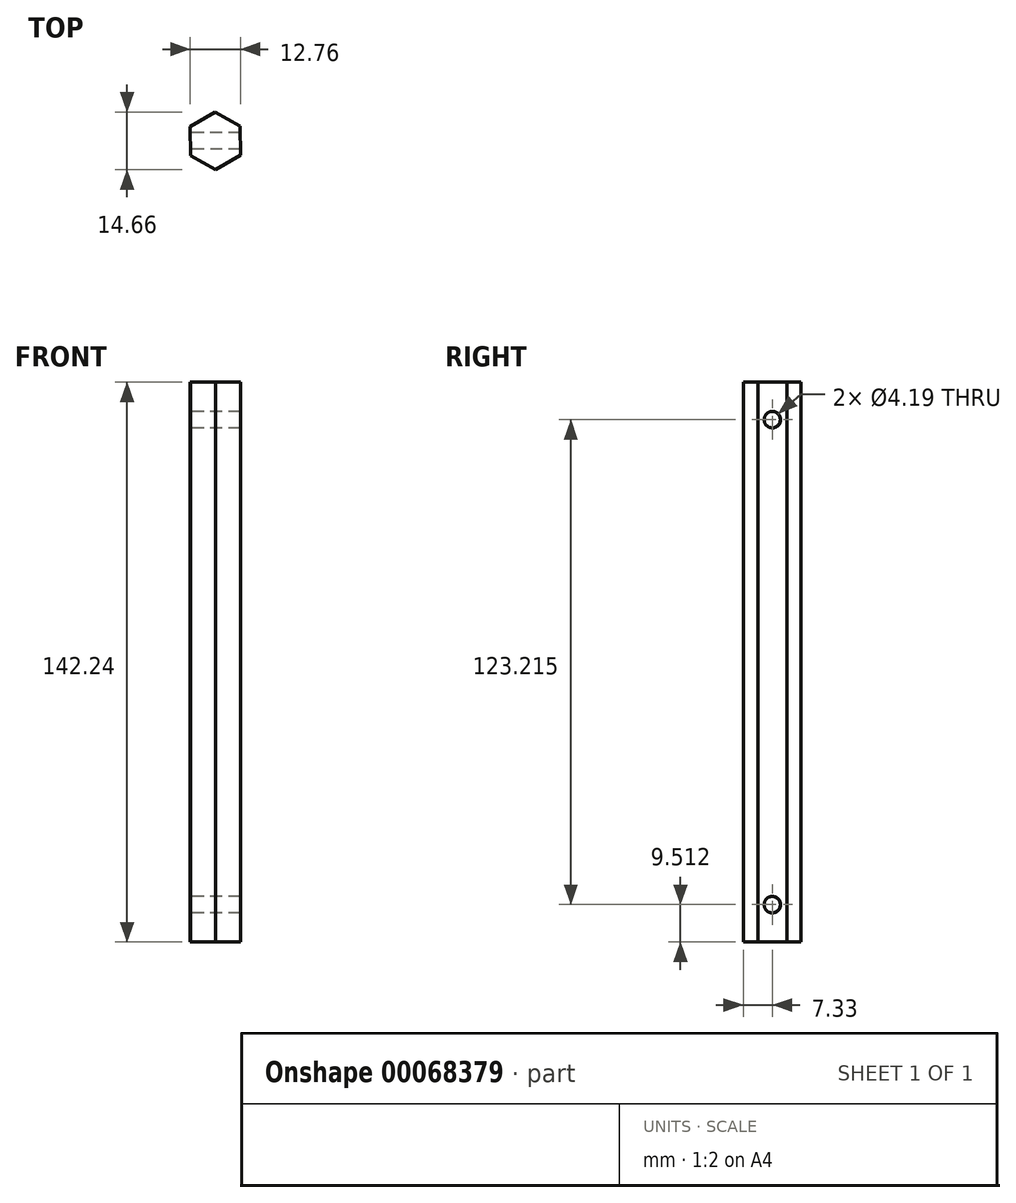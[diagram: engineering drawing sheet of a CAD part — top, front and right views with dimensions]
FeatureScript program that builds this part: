
annotation { "Feature Type Name" : "Feature", "Feature Type Description" : "" }
export const myFeature = defineFeature(function(context is Context, id is Id, definition is map)
    precondition{}
    {
        {
            var Q0;
            Q0=qCreatedBy(makeId("Top.planeOp"),FACE);
            var sketch = newSketch(context, id + "F0", { "sketchPlane" : qUnion([Q0])});
            skCircle(sketch, "E0.cCircle", {"center": v(0, 0) * mm, "radius": 6.35 * mm, "construction": true});
            skLineSegment(sketch, "E0.0", {"start": v(6.38, -3.62) * mm, "end": v(0.05, -7.33) * mm});
            skLineSegment(sketch, "E0.1", {"start": v(0.05, -7.33) * mm, "end": v(-6.32, -3.71) * mm});
            skLineSegment(sketch, "E0.2", {"start": v(-6.32, -3.71) * mm, "end": v(-6.38, 3.62) * mm});
            skLineSegment(sketch, "E0.3", {"start": v(-6.38, 3.62) * mm, "end": v(-0.05, 7.33) * mm});
            skLineSegment(sketch, "E0.4", {"start": v(-0.05, 7.33) * mm, "end": v(6.32, 3.71) * mm});
            skLineSegment(sketch, "E0.5", {"start": v(6.32, 3.71) * mm, "end": v(6.38, -3.62) * mm});
            skPoint(sketch, "E0.0.midPoint", {"position": v(3.22, -5.48) * mm});
            skSolve(sketch);
        }
        {
            var Q0;
            Q0=makeQuery(id+"F0.imprint","IMPRINT",FACE,{"disambiguationData":[TD([[makeQuery(id+"F0.imprint","IMPRINT",EDGE,{"derivedFrom":sQuery(id+"F0.wireOp",EDGE,"E0.0")}),-1.0]])]});
            extrude(context, id + "F1", {"entities" : qUnion([Q0]), "depth" : 142.24 * mm});
        }
        {
            var Q0;
            Q0=makeQuery(id+"F1.opExtrude","SWEPT_FACE",FACE,{"disambiguationData":[OSD([sQuery(id+"F0.wireOp",EDGE,"E0.2")])]});
            var sketch = newSketch(context, id + "F2", { "sketchPlane" : qUnion([Q0])});
            skCircle(sketch, "E1", {"center": v(0, 9.51) * mm, "radius": 2.1 * mm});
            skCircle(sketch, "E2", {"center": v(0, 132.73) * mm, "radius": 2.1 * mm});
            skPoint(sketch, "E2.centerSnap0", {"position": v(0, 142.24) * mm});
            skSolve(sketch);
        }
        {
            var Q0;
            Q0=makeQuery(id+"F2.imprint","IMPRINT",FACE,{"disambiguationData":[TD([[makeQuery(id+"F2.imprint","IMPRINT",EDGE,{"derivedFrom":sQuery(id+"F2.wireOp",EDGE,"E2")}),1.0]])]});
            var Q1;
            Q1=makeQuery(id+"F2.imprint","IMPRINT",FACE,{"disambiguationData":[TD([[makeQuery(id+"F2.imprint","IMPRINT",EDGE,{"derivedFrom":sQuery(id+"F2.wireOp",EDGE,"E1")}),1.0]])]});
            extrude(context, id + "F3", {"entities" : qUnion([Q0, Q1]), "operationType" : NewBodyOperationType.REMOVE, "oppositeDirection" : true, "depth" : 12.7 * mm});
        }
    });
